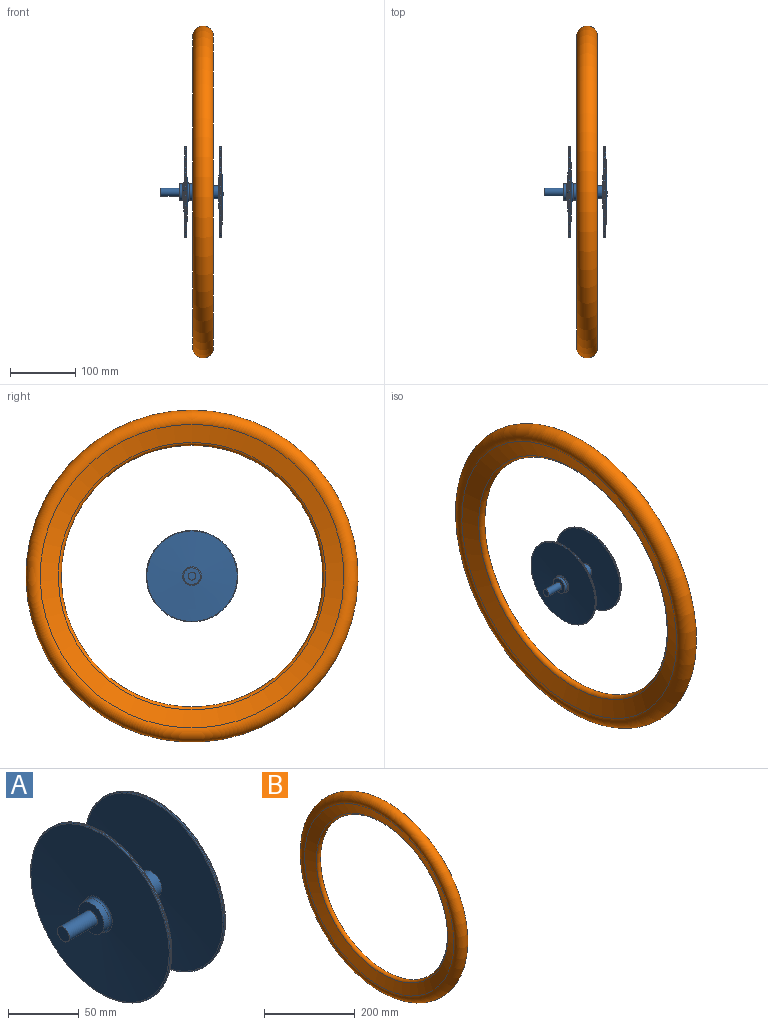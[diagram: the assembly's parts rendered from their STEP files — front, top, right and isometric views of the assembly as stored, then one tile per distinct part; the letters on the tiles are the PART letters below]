
ASSEMBLY  parts=2 mates=2
PART A: 20 faces, bbox 95.3x151.5x151.5 mm
  f0: plane 12x12mm, normal (-1,0,0), area 113.1mm2, adj f12
  f1: cone r=69.84mm half-angle=88deg, axis (-1,0,0), area 15008.2mm2, adj f13
  f2: cone r=69.92mm half-angle=2deg, axis (-1,0,0), area 364.7mm2, adj f13,f14
  f3: cone r=10.16mm half-angle=88deg, axis (1,0,0), area 14696.3mm2, adj f4,f14
  f4: cylinder r=10.16mm len=20.32mm, axis (-1,0,0), area 702.2mm2, adj f3,f5
  f5: cone r=12.7mm half-angle=32.8deg, axis (-1,0,0), area 264.2mm2, adj f4,f17
  f6: cylinder r=12.7mm len=28.29mm, axis (-1,0,0), area 2257.8mm2, adj f17,f18
  f7: cone r=69.92mm half-angle=88deg, axis (-1,0,0), area 14262.8mm2, adj f15,f18
  f8: cone r=70mm half-angle=2deg, axis (-1,0,0), area 365.1mm2, adj f15,f16
  f9: cone r=12.7mm half-angle=88deg, axis (1,0,0), area 14421mm2, adj f16,f19
  f10: cylinder r=12.7mm len=25.4mm, axis (-1,0,0), area 417.1mm2, adj f11,f19
  f11: plane 25.4x25.4mm, normal (-1,0,0), area 393.6mm2, adj f10,f12
  f12: cylinder r=6mm len=28.02mm, axis (-1,0,0), area 1056.1mm2, adj f0,f11
  f13: torus R=69.07mm, axis (1,0,0), area 520mm2, adj f1,f2
  f14: torus R=69.1mm, axis (1,0,0), area 544.5mm2, adj f2,f3
  f15: torus R=69.15mm, axis (1,0,0), area 520.6mm2, adj f7,f8
  f16: torus R=69.18mm, axis (1,0,0), area 545.2mm2, adj f8,f9
  f17: torus R=9.53mm, axis (1,0,0), area 142.9mm2, adj f5,f6
  f18: torus R=15.88mm, axis (-1,0,0), area 423.1mm2, adj f6,f7
  f19: torus R=14.27mm, axis (-1,0,0), area 201.4mm2, adj f9,f10
PART B: 4 faces, bbox 29.4x549.9x549.9 mm
  f0: cone r=232.16mm half-angle=72.6deg, axis (-1,0,0), area 39781.4mm2, adj f1,f3
  f1: torus R=206.38mm, axis (-1,0,0), area 20395.7mm2, adj f0,f2
  f2: cone r=232.16mm half-angle=72.6deg, axis (1,0,0), area 39781.4mm2, adj f1,f3
  f3: torus R=238.12mm, axis (-1,0,0), area 95849.9mm2, adj f0,f2
PLACE A t=(-62.13,0.49,-1.35)mm
PLACE B t=(2.41,0.49,-1.35)mm
MATE revolute A.f4 <-> B.f0  axis (-1,0,0) through (-21.11,0.49,-1.35)mm
MATE parallel A.f4 <-> B.f0  axis (-1,0,0) through (-62.13,0.49,-1.35)mm
